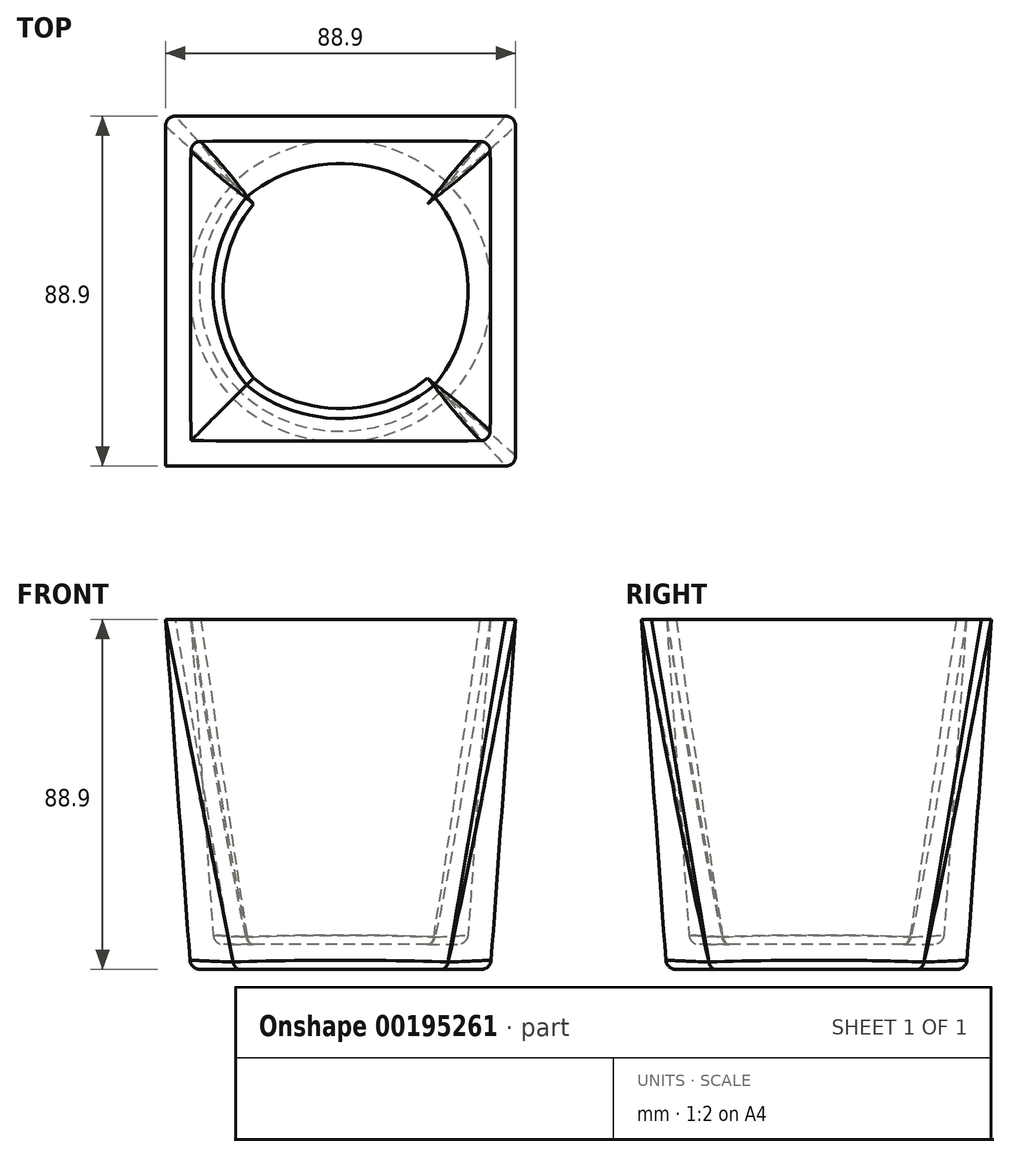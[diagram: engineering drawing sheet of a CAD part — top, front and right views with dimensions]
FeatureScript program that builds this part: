
annotation { "Feature Type Name" : "Feature", "Feature Type Description" : "" }
export const myFeature = defineFeature(function(context is Context, id is Id, definition is map)
    precondition{}
    {
        {
            var Q0;
            Q0=qCreatedBy(makeId("Top.planeOp"),FACE);
            var sketch = newSketch(context, id + "F0", { "sketchPlane" : qUnion([Q0])});
            skCircle(sketch, "E0", {"center": v(0, 0) * mm, "radius": 38.1 * mm});
            skSolve(sketch);
        }
        {
            var Q0;
            Q0=makeQuery(id+"F0.imprint","IMPRINT",FACE,{"disambiguationData":[TD([[makeQuery(id+"F0.imprint","IMPRINT",EDGE,{"derivedFrom":sQuery(id+"F0.wireOp",EDGE,"E0")}),1.0]])]});
            extrude(context, id + "F1", {"entities" : qUnion([Q0]), "depth" : 88.9 * mm});
        }
        {
            var Q0;
            Q0=makeQuery(id+"F1.opExtrude","CAP_FACE",FACE,{"disambiguationData":[OSD([sQuery(id+"F0.wireOp",EDGE,"E0")])],"isStart":false});
            var sketch = newSketch(context, id + "F2", { "sketchPlane" : qUnion([Q0])});
            skLineSegment(sketch, "E1.bottom", {"start": v(44.45, -44.45) * mm, "end": v(-44.45, -44.45) * mm});
            skLineSegment(sketch, "E1.top", {"start": v(44.45, 44.45) * mm, "end": v(-44.45, 44.45) * mm});
            skLineSegment(sketch, "E1.left", {"start": v(44.45, -44.45) * mm, "end": v(44.45, 44.45) * mm});
            skLineSegment(sketch, "E1.right", {"start": v(-44.45, -44.45) * mm, "end": v(-44.45, 44.45) * mm});
            skPoint(sketch, "E1.middle", {"position": v(0, 0) * mm});
            skSolve(sketch);
        }
        {
            var Q1;
            Q1 = qSketchRegion(id + "F2", true);
            var Q2;
            Q2 = qSketchRegion(id + "F0", true);
            loft(context, id + "F3", {"operationType" : NewBodyOperationType.ADD, "sheetProfilesArray" : [{ "sheetProfileEntities" : qUnion([Q1]) }, { "sheetProfileEntities" : qUnion([Q2]) }]});
        }
        {
            var Q0;
            {var subQ0=sQuery(id+"F0.wireOp",EDGE,"E0");Q0=makeQuery(id+"F3.boolean.opBoolean","MERGE",FACE,{"derivedFrom":[makeQuery(id+"F1.opExtrude","CAP_FACE",FACE,{"disambiguationData":[OSD([subQ0])],"isStart":false}),makeQuery(id+"F3.opLoft","CAP_FACE",FACE,{"disambiguationData":[OSD([makeQuery(id+"F2.imprint","IMPRINT",FACE,{"disambiguationData":[TD([[makeQuery(id+"F2.imprint","IMPRINT",EDGE,{"derivedFrom":makeQuery(id+"F1.opExtrude","CAP_EDGE",EDGE,{"disambiguationData":[OSD([subQ0])],"isStart":false})}),1.0]])]})])],"isStart":true})]});}
            shell(context, id + "F4", {"entities" : qUnion([Q0]), "thickness" : 6.35 * mm});
        }
        {
            var Q0;
            {var subQ0=sQuery(id+"F2.wireOp",EDGE,"E1.right");var subQ1=sQuery(id+"F2.wireOp",EDGE,"E1.top");var subQ2=sQuery(id+"F2.wireOp",EDGE,"E1.bottom");var subQ3=sQuery(id+"F0.wireOp",EDGE,"E0");Q0=makeQuery(id+"F4.opShell","OFFSET_EDGE",EDGE,{"disambiguationData":[OSD([subQ3,subQ2,subQ1,subQ0]),TDD([makeQuery(id+"F3.opLoft","SWEPT_EDGE",EDGE,{"disambiguationData":[OSD([subQ3,subQ2,subQ1,subQ0])]})])]});}
            var Q1;
            Q1=makeQuery(id+"F4.opShell","OFFSET_EDGE",EDGE,{"disambiguationData":[OSD([sQuery(id+"F0.wireOp",EDGE,"E0"),sQuery(id+"F2.wireOp",EDGE,"E1.top"),sQuery(id+"F2.wireOp",EDGE,"E1.left"),sQuery(id+"F2.wireOp",EDGE,"E1.right")])]});
            var Q2;
            Q2=makeQuery(id+"F4.opShell","OFFSET_EDGE",EDGE,{"disambiguationData":[OSD([sQuery(id+"F2.wireOp",EDGE,"E1.bottom"),sQuery(id+"F2.wireOp",EDGE,"E1.left")])]});
            var Q3;
            {var subQ0=sQuery(id+"F2.wireOp",EDGE,"E1.right");var subQ1=sQuery(id+"F2.wireOp",EDGE,"E1.left");var subQ2=sQuery(id+"F2.wireOp",EDGE,"E1.bottom");var subQ3=sQuery(id+"F0.wireOp",EDGE,"E0");Q3=makeQuery(id+"F4.opShell","OFFSET_EDGE",EDGE,{"disambiguationData":[OSD([subQ3,subQ2,subQ1,subQ0]),TDD([makeQuery(id+"F3.opLoft","SWEPT_EDGE",EDGE,{"disambiguationData":[OSD([subQ3,subQ2,subQ1,subQ0])]})])]});}
            var Q4;
            Q4=makeQuery(id+"F4.opShell","OFFSET_FACE",FACE,{"disambiguationData":[OSD([sQuery(id+"F0.wireOp",EDGE,"E0")])]});
            var Q5;
            Q5=makeQuery(id+"F3.opLoft","SWEPT_EDGE",EDGE,{"disambiguationData":[OSD([sQuery(id+"F2.wireOp",EDGE,"E1.bottom"),sQuery(id+"F2.wireOp",EDGE,"E1.left")])]});
            var Q6;
            Q6=makeQuery(id+"F3.opLoft","SWEPT_EDGE",EDGE,{"disambiguationData":[OSD([sQuery(id+"F0.wireOp",EDGE,"E0"),sQuery(id+"F2.wireOp",EDGE,"E1.bottom"),sQuery(id+"F2.wireOp",EDGE,"E1.left"),sQuery(id+"F2.wireOp",EDGE,"E1.right")])]});
            var Q7;
            Q7=makeQuery(id+"F3.opLoft","SWEPT_EDGE",EDGE,{"disambiguationData":[OSD([sQuery(id+"F0.wireOp",EDGE,"E0"),sQuery(id+"F2.wireOp",EDGE,"E1.top"),sQuery(id+"F2.wireOp",EDGE,"E1.left"),sQuery(id+"F2.wireOp",EDGE,"E1.right")])]});
            var Q8;
            Q8=makeQuery(id+"F3.opLoft","SWEPT_EDGE",EDGE,{"disambiguationData":[OSD([sQuery(id+"F0.wireOp",EDGE,"E0"),sQuery(id+"F2.wireOp",EDGE,"E1.bottom"),sQuery(id+"F2.wireOp",EDGE,"E1.top"),sQuery(id+"F2.wireOp",EDGE,"E1.right")])]});
            var Q9;
            Q9=makeQuery(id+"F1.opExtrude","CAP_FACE",FACE,{"disambiguationData":[OSD([sQuery(id+"F0.wireOp",EDGE,"E0")])],"isStart":true});
            fillet(context, id + "F5", {"entities" : qUnion([Q0, Q1, Q2, Q3, Q4, Q5, Q6, Q7, Q8, Q9]), "radius" : 2.54 * mm, "tangentPropagation" : true, "allowEdgeOverflow" : false});
        }
    });
